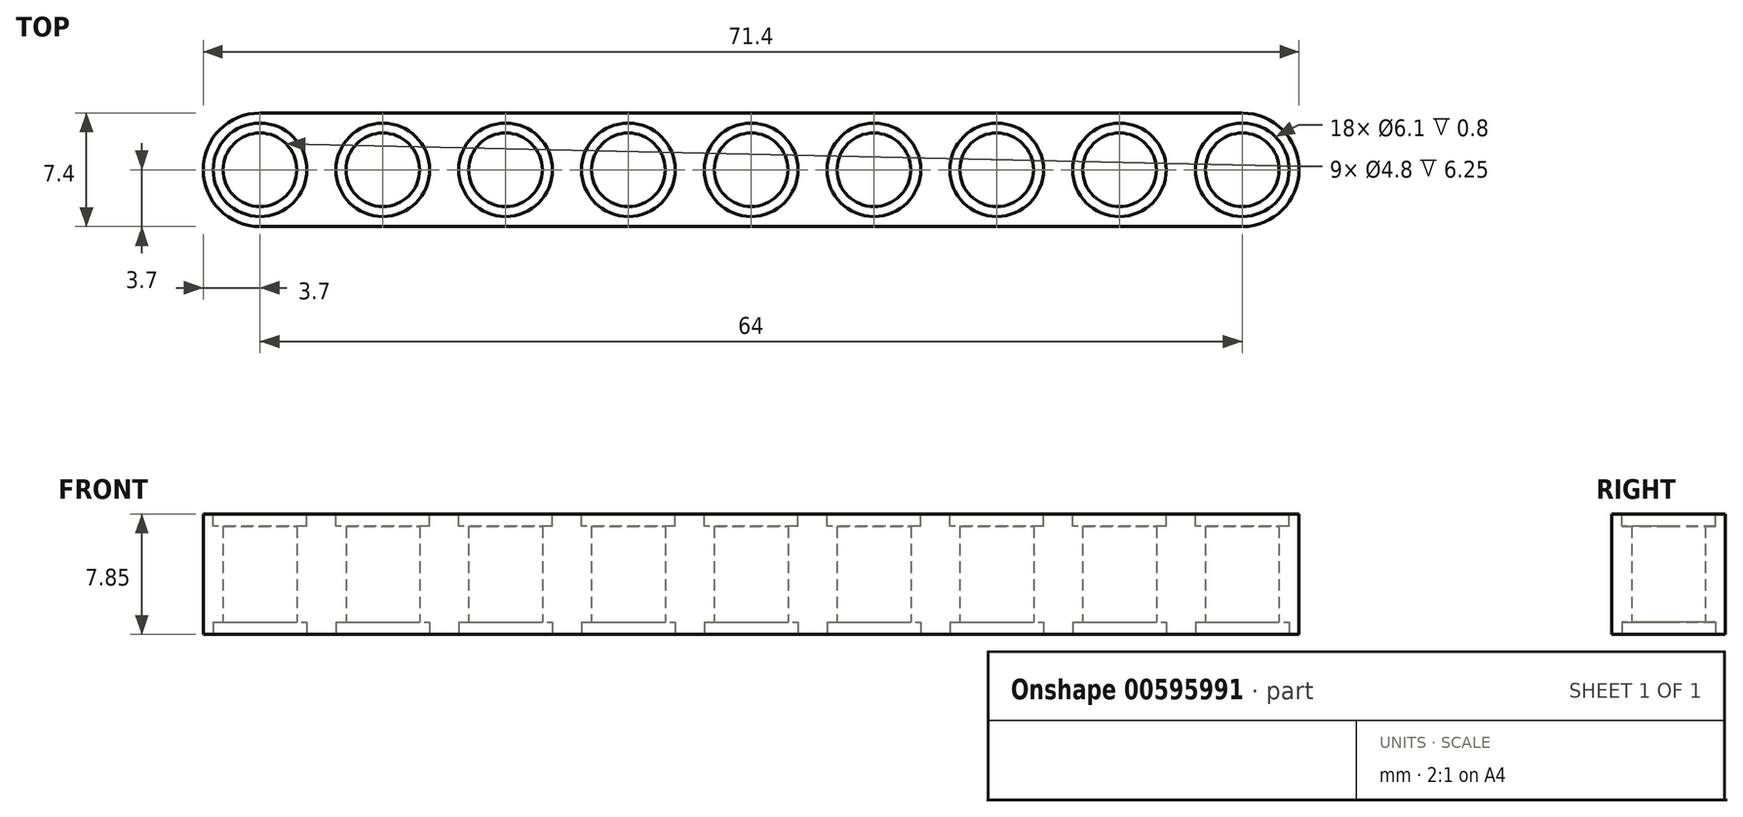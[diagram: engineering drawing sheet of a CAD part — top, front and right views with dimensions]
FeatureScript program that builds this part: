
annotation { "Feature Type Name" : "Feature", "Feature Type Description" : "" }
export const myFeature = defineFeature(function(context is Context, id is Id, definition is map)
    precondition{}
    {
        {
            var Q0;
            Q0=qCreatedBy(makeId("Top.planeOp"),FACE);
            var sketch = newSketch(context, id + "F0", { "sketchPlane" : qUnion([Q0])});
            skLineSegment(sketch, "E0", {"start": v(0, 0) * mm, "end": v(64, 0) * mm});
            skLineSegment(sketch, "E1", {"start": v(0, 7.4) * mm, "end": v(64, 7.4) * mm});
            skArc(sketch, "E2", {"start": v(64, 7.4) * mm, "mid": v(67.7, 3.7) * mm, "end": v(64, 0) * mm});
            skArc(sketch, "E3", {"start": v(0, 7.4) * mm, "mid": v(-3.7, 3.7) * mm, "end": v(0, 0) * mm});
            skCircle(sketch, "E4", {"center": v(0, 3.7) * mm, "radius": 2.4 * mm});
            skCircle(sketch, "E5.1.0.0", {"center": v(8, 3.7) * mm, "radius": 2.4 * mm});
            skCircle(sketch, "E5.2.0.0", {"center": v(16, 3.7) * mm, "radius": 2.4 * mm});
            skCircle(sketch, "E5.3.0.0", {"center": v(24, 3.7) * mm, "radius": 2.4 * mm});
            skCircle(sketch, "E5.4.0.0", {"center": v(32, 3.7) * mm, "radius": 2.4 * mm});
            skCircle(sketch, "E5.5.0.0", {"center": v(40, 3.7) * mm, "radius": 2.4 * mm});
            skCircle(sketch, "E5.6.0.0", {"center": v(48, 3.7) * mm, "radius": 2.4 * mm});
            skCircle(sketch, "E5.7.0.0", {"center": v(56, 3.7) * mm, "radius": 2.4 * mm});
            skCircle(sketch, "E5.8.0.0", {"center": v(64, 3.7) * mm, "radius": 2.4 * mm});
            skLineSegment(sketch, "E5.direction1", {"start": v(0, 3.7) * mm, "end": v(8, 3.7) * mm, "construction": true});
            skSolve(sketch);
        }
        {
            var Q0;
            Q0=qSketchRegion(id+"F0",true);
            extrude(context, id + "F1", {"entities" : qUnion([Q0]), "depth" : 7.85 * mm, "offsetDistance" : 25 * mm});
        }
        {
            var Q0;
            Q0=makeQuery(id+"F1.opExtrude","CAP_FACE",FACE,{"disambiguationData":[OSD([sQuery(id+"F0.wireOp",EDGE,"E0"),sQuery(id+"F0.wireOp",EDGE,"E1"),sQuery(id+"F0.wireOp",EDGE,"E2"),sQuery(id+"F0.wireOp",EDGE,"E3"),sQuery(id+"F0.wireOp",EDGE,"E4"),sQuery(id+"F0.wireOp",EDGE,"E5.1.0.0"),sQuery(id+"F0.wireOp",EDGE,"E5.2.0.0"),sQuery(id+"F0.wireOp",EDGE,"E5.3.0.0"),sQuery(id+"F0.wireOp",EDGE,"E5.4.0.0"),sQuery(id+"F0.wireOp",EDGE,"E5.5.0.0"),sQuery(id+"F0.wireOp",EDGE,"E5.6.0.0"),sQuery(id+"F0.wireOp",EDGE,"E5.7.0.0"),sQuery(id+"F0.wireOp",EDGE,"E5.8.0.0")])],"isStart":false});
            var sketch = newSketch(context, id + "F2", { "sketchPlane" : qUnion([Q0])});
            skCircle(sketch, "E6.0", {"center": v(0, 3.7) * mm, "radius": 2.4 * mm, "construction": true});
            skCircle(sketch, "E7.0", {"center": v(8, 3.7) * mm, "radius": 2.4 * mm, "construction": true});
            skCircle(sketch, "E8.0", {"center": v(16, 3.7) * mm, "radius": 2.4 * mm, "construction": true});
            skCircle(sketch, "E9.0", {"center": v(24, 3.7) * mm, "radius": 2.4 * mm, "construction": true});
            skCircle(sketch, "E10.0", {"center": v(32, 3.7) * mm, "radius": 2.4 * mm, "construction": true});
            skCircle(sketch, "E11.0", {"center": v(40, 3.7) * mm, "radius": 2.4 * mm, "construction": true});
            skCircle(sketch, "E12.0", {"center": v(48, 3.7) * mm, "radius": 2.4 * mm, "construction": true});
            skCircle(sketch, "E13.0", {"center": v(56, 3.7) * mm, "radius": 2.4 * mm, "construction": true});
            skCircle(sketch, "E14.0", {"center": v(64, 3.7) * mm, "radius": 2.4 * mm, "construction": true});
            skCircle(sketch, "E15.0", {"center": v(0, 3.7) * mm, "radius": 3.05 * mm});
            skCircle(sketch, "E16.0", {"center": v(8, 3.7) * mm, "radius": 3.05 * mm});
            skCircle(sketch, "E17.0", {"center": v(16, 3.7) * mm, "radius": 3.05 * mm});
            skCircle(sketch, "E18.0", {"center": v(24, 3.7) * mm, "radius": 3.05 * mm});
            skCircle(sketch, "E19.0", {"center": v(32, 3.7) * mm, "radius": 3.05 * mm});
            skCircle(sketch, "E20.0", {"center": v(40, 3.7) * mm, "radius": 3.05 * mm});
            skCircle(sketch, "E21.0", {"center": v(48, 3.7) * mm, "radius": 3.05 * mm});
            skCircle(sketch, "E22.0", {"center": v(56, 3.7) * mm, "radius": 3.05 * mm});
            skCircle(sketch, "E23.0", {"center": v(64, 3.7) * mm, "radius": 3.05 * mm});
            skSolve(sketch);
        }
        {
            var Q0;
            Q0=qSketchRegion(id+"F2",true);
            extrude(context, id + "F3", {"entities" : qUnion([Q0]), "operationType" : NewBodyOperationType.REMOVE, "oppositeDirection" : true, "depth" : 0.8 * mm, "offsetDistance" : 25 * mm});
        }
        {
            var Q0;
            Q0=makeQuery(id+"F1.opExtrude","CAP_FACE",FACE,{"disambiguationData":[OSD([sQuery(id+"F0.wireOp",EDGE,"E0"),sQuery(id+"F0.wireOp",EDGE,"E1"),sQuery(id+"F0.wireOp",EDGE,"E2"),sQuery(id+"F0.wireOp",EDGE,"E3"),sQuery(id+"F0.wireOp",EDGE,"E4"),sQuery(id+"F0.wireOp",EDGE,"E5.1.0.0"),sQuery(id+"F0.wireOp",EDGE,"E5.2.0.0"),sQuery(id+"F0.wireOp",EDGE,"E5.3.0.0"),sQuery(id+"F0.wireOp",EDGE,"E5.4.0.0"),sQuery(id+"F0.wireOp",EDGE,"E5.5.0.0"),sQuery(id+"F0.wireOp",EDGE,"E5.6.0.0"),sQuery(id+"F0.wireOp",EDGE,"E5.7.0.0"),sQuery(id+"F0.wireOp",EDGE,"E5.8.0.0")])],"isStart":true});
            var sketch = newSketch(context, id + "F4", { "sketchPlane" : qUnion([Q0])});
            skCircle(sketch, "E24.0", {"center": v(0, -3.7) * mm, "radius": 3.05 * mm});
            skCircle(sketch, "E24.1", {"center": v(8, -3.7) * mm, "radius": 3.05 * mm});
            skCircle(sketch, "E25.0", {"center": v(16, -3.7) * mm, "radius": 3.05 * mm});
            skCircle(sketch, "E26.0", {"center": v(24, -3.7) * mm, "radius": 3.05 * mm});
            skCircle(sketch, "E27.0", {"center": v(32, -3.7) * mm, "radius": 3.05 * mm});
            skCircle(sketch, "E28.0", {"center": v(64, -3.7) * mm, "radius": 3.05 * mm});
            skCircle(sketch, "E28.1", {"center": v(56, -3.7) * mm, "radius": 3.05 * mm});
            skCircle(sketch, "E28.2", {"center": v(40, -3.7) * mm, "radius": 3.05 * mm});
            skCircle(sketch, "E28.3", {"center": v(48, -3.7) * mm, "radius": 3.05 * mm});
            skSolve(sketch);
        }
        {
            var Q0;
            Q0=qSketchRegion(id+"F4",true);
            extrude(context, id + "F5", {"entities" : qUnion([Q0]), "operationType" : NewBodyOperationType.REMOVE, "oppositeDirection" : true, "depth" : 0.8 * mm, "offsetDistance" : 25 * mm});
        }
    });
